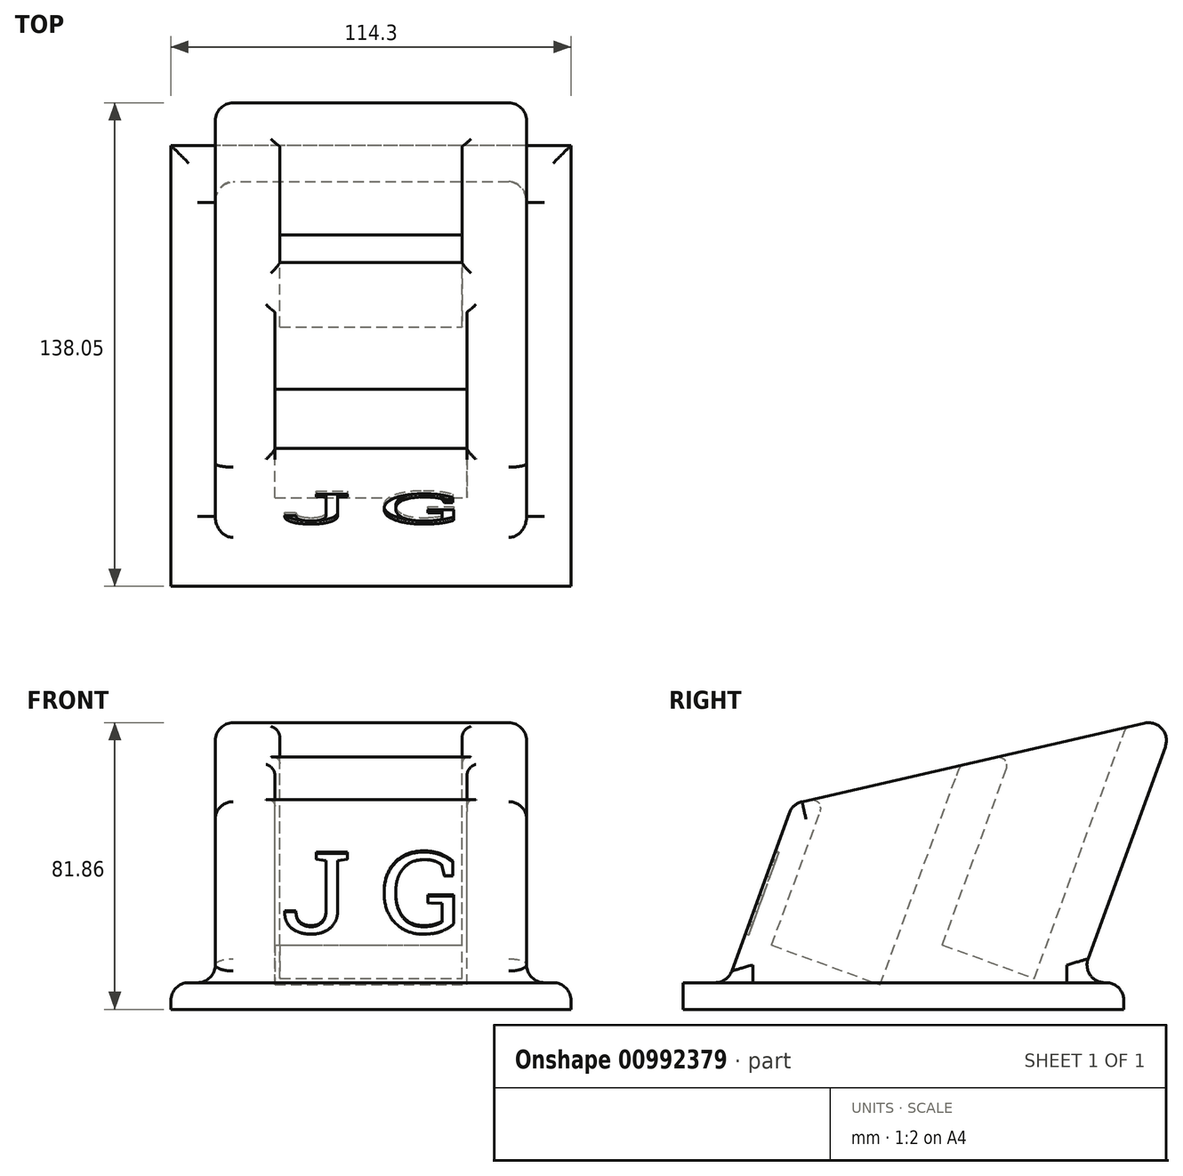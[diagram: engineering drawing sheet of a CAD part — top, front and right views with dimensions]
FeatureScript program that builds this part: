
annotation { "Feature Type Name" : "Feature", "Feature Type Description" : "" }
export const myFeature = defineFeature(function(context is Context, id is Id, definition is map)
    precondition{}
    {
        {
            var Q0;
            Q0=qCreatedBy(makeId("Right.planeOp"),FACE);
            var sketch = newSketch(context, id + "F0", { "sketchPlane" : qUnion([Q0])});
            skLineSegment(sketch, "E0.bottom", {"start": v(-88.9, 0) * mm, "end": v(88.9, 0) * mm});
            skLineSegment(sketch, "E0.left", {"start": v(-88.9, 0) * mm, "end": v(-88.9, 7.62) * mm});
            skLineSegment(sketch, "E0.right", {"start": v(88.9, 0) * mm, "end": v(88.9, 7.62) * mm});
            skLineSegment(sketch, "E1", {"start": v(-88.9, 7.62) * mm, "end": v(88.9, 7.62) * mm});
            skLineSegment(sketch, "E2", {"start": v(76.2, 7.62) * mm, "end": v(103.93, 83.82) * mm});
            skLineSegment(sketch, "E3", {"start": v(-76.2, 7.62) * mm, "end": v(-62.33, 45.72) * mm});
            skLineSegment(sketch, "E4", {"start": v(-62.33, 45.72) * mm, "end": v(103.93, 83.82) * mm});
            skSolve(sketch);
        }
        {
            var Q0;
            Q0=makeQuery(id+"F0.imprint","IMPRINT",FACE,{"disambiguationData":[TD([[makeQuery(id+"F0.imprint","IMPRINT",EDGE,{"derivedFrom":sQuery(id+"F0.wireOp",EDGE,"E0.bottom")}),1.0]])]});
            extrude(context, id + "F1", {"entities" : qUnion([Q0]), "depth" : 114.3 * mm, "offsetDistance" : 25.4 * mm, "symmetric" : true});
        }
        {
            var Q0;
            {var subQ0=sQuery(id+"F0.wireOp",EDGE,"E2");Q0=makeQuery(id+"F0.imprint","IMPRINT",FACE,{"disambiguationData":[TD([[makeQuery(id+"F0.imprint","IMPRINT",EDGE,{"derivedFrom":subQ0}),1.0]])]});}
            extrude(context, id + "F2", {"entities" : qUnion([Q0]), "operationType" : NewBodyOperationType.ADD, "depth" : 88.9 * mm, "offsetDistance" : 25.4 * mm, "symmetric" : true});
        }
        {
            var Q0;
            Q0=makeQuery(id+"F2.opExtrude","SWEPT_EDGE",EDGE,{"disambiguationData":[OSD([sQuery(id+"F0.wireOp",EDGE,"E2"),sQuery(id+"F0.wireOp",EDGE,"E4")])]});
            var Q1;
            Q1=sQuery(id+"F0.wireOp",EDGE,"E2");
            cPlane(context, id + "F3", {"entities" : qUnion([Q0, Q1]), "cplaneType" : CPlaneType.LINE_ANGLE, "offset" : 25.4 * mm, "angle" : 90 * degree, "width" : 152.4 * mm, "height" : 152.4 * mm});
        }
        {
            var Q0;
            Q0=makeQuery(id+"F2.opExtrude","SWEPT_FACE",FACE,{"disambiguationData":[OSD([sQuery(id+"F0.wireOp",EDGE,"E4")])]});
            var sketch = newSketch(context, id + "F4", { "sketchPlane" : qUnion([Q0])});
            skLineSegment(sketch, "E5.bottom", {"start": v(20.96, -42.93) * mm, "end": v(-20.96, -42.93) * mm});
            skSolve(sketch);
        }
        {
            var Q0;
            Q0=qCreatedBy(id+"F3.planeOp",FACE);
            var sketch = newSketch(context, id + "F5", { "sketchPlane" : qUnion([Q0])});
            skLineSegment(sketch, "E6.0", {"start": v(20.96, 67.81) * mm, "end": v(-20.96, 67.81) * mm});
            skLineSegment(sketch, "E7", {"start": v(-20.96, 67.81) * mm, "end": v(-20.96, 59.43) * mm});
            skLineSegment(sketch, "E8", {"start": v(-20.96, 59.43) * mm, "end": v(20.96, 59.43) * mm});
            skLineSegment(sketch, "E9", {"start": v(20.95, 59.43) * mm, "end": v(20.95, 67.81) * mm});
            skSolve(sketch);
        }
        {
            var Q0;
            Q0 = qSketchRegion(id + "F5", true);
            extrude(context, id + "F6", {"entities" : qUnion([Q0]), "operationType" : NewBodyOperationType.REMOVE, "depth" : 110.74 * mm, "offsetDistance" : 25.4 * mm});
        }
        {
            var Q0;
            {var subQ0=sQuery(id+"F0.wireOp",EDGE,"E4");Q0=makeQuery(id+"F4.imprint","IMPRINT",FACE,{"disambiguationData":[TD([[makeQuery(id+"F4.imprint","IMPRINT",EDGE,{"derivedFrom":makeQuery(id+"F2.opExtrude","CAP_EDGE",EDGE,{"disambiguationData":[OSD([subQ0])],"isStart":true})}),-1.0]])]});}
            var sketch = newSketch(context, id + "F7", { "sketchPlane" : qUnion([Q0])});
            skLineSegment(sketch, "E10", {"start": v(-23.5, -20.24) * mm, "end": v(23.5, -20.24) * mm});
            skSolve(sketch);
        }
        {
            var Q0;
            Q0=qCreatedBy(id+"F3.planeOp",FACE);
            var sketch = newSketch(context, id + "F8", { "sketchPlane" : qUnion([Q0])});
            skLineSegment(sketch, "E11.0", {"start": v(-23.5, 48.77) * mm, "end": v(23.5, 48.77) * mm});
            skLineSegment(sketch, "E12", {"start": v(-23.5, 48.77) * mm, "end": v(-23.5, 27.94) * mm});
            skLineSegment(sketch, "E13", {"start": v(-23.5, 27.94) * mm, "end": v(23.5, 27.94) * mm});
            skLineSegment(sketch, "E14", {"start": v(23.5, 27.94) * mm, "end": v(23.5, 48.77) * mm});
            skSolve(sketch);
        }
        {
            var Q0;
            Q0 = qSketchRegion(id + "F8", true);
            extrude(context, id + "F9", {"entities" : qUnion([Q0]), "operationType" : NewBodyOperationType.REMOVE, "depth" : 112.27 * mm, "offsetDistance" : 25.4 * mm});
        }
        {
            var Q0;
            {var subQ0=sQuery(id+"F0.wireOp",EDGE,"E4");Q0=makeQuery(id+"F4.imprint","IMPRINT",FACE,{"disambiguationData":[TD([[makeQuery(id+"F4.imprint","IMPRINT",EDGE,{"derivedFrom":makeQuery(id+"F2.opExtrude","CAP_EDGE",EDGE,{"disambiguationData":[OSD([subQ0])],"isStart":true})}),-1.0]])]});}
            var sketch = newSketch(context, id + "F10", { "sketchPlane" : qUnion([Q0])});
            skLineSegment(sketch, "E15", {"start": v(-27.43, 17.27) * mm, "end": v(27.43, 17.27) * mm});
            skLineSegment(sketch, "E16", {"start": v(0, 85.1) * mm, "end": v(0, -16.61) * mm, "construction": true});
            skSolve(sketch);
        }
        {
            var Q0;
            Q0=qCreatedBy(id+"F3.planeOp",FACE);
            var sketch = newSketch(context, id + "F11", { "sketchPlane" : qUnion([Q0])});
            skLineSegment(sketch, "E17.0", {"start": v(-27.43, 17.28) * mm, "end": v(27.43, 17.28) * mm});
            skLineSegment(sketch, "E18", {"start": v(-27.43, 17.28) * mm, "end": v(-27.43, -15.74) * mm});
            skLineSegment(sketch, "E19", {"start": v(-27.43, -15.74) * mm, "end": v(27.43, -15.74) * mm});
            skLineSegment(sketch, "E20", {"start": v(27.43, -15.74) * mm, "end": v(27.43, 17.28) * mm});
            skSolve(sketch);
        }
        {
            var Q0;
            Q0 = qSketchRegion(id + "F11", true);
            extrude(context, id + "F12", {"entities" : qUnion([Q0]), "operationType" : NewBodyOperationType.REMOVE, "depth" : 101.1 * mm, "offsetDistance" : 25.4 * mm});
        }
        {
            var Q0;
            {var subQ0=sQuery(id+"F0.wireOp",EDGE,"E4");Q0=makeQuery(id+"F4.imprint","IMPRINT",FACE,{"disambiguationData":[TD([[makeQuery(id+"F4.imprint","IMPRINT",EDGE,{"derivedFrom":makeQuery(id+"F2.opExtrude","CAP_EDGE",EDGE,{"disambiguationData":[OSD([subQ0])],"isStart":true})}),-1.0]])]});}
            var sketch = newSketch(context, id + "F13", { "sketchPlane" : qUnion([Q0])});
            skLineSegment(sketch, "E21", {"start": v(-26.04, 71.84) * mm, "end": v(26.04, 71.84) * mm});
            skSolve(sketch);
        }
        {
            var Q0;
            Q0=qCreatedBy(id+"F3.planeOp",FACE);
            var sketch = newSketch(context, id + "F14", { "sketchPlane" : qUnion([Q0])});
            skLineSegment(sketch, "E22.0", {"start": v(-26.04, -28.54) * mm, "end": v(26.04, -28.54) * mm});
            skLineSegment(sketch, "E23", {"start": v(-26.03, -28.54) * mm, "end": v(-26.03, -56.48) * mm});
            skLineSegment(sketch, "E24", {"start": v(-26.03, -56.48) * mm, "end": v(26.04, -56.48) * mm});
            skLineSegment(sketch, "E25", {"start": v(26.04, -56.48) * mm, "end": v(26.04, -28.54) * mm});
            skSolve(sketch);
        }
        {
            var Q0;
            Q0 = qSketchRegion(id + "F14", true);
            extrude(context, id + "F15", {"entities" : qUnion([Q0]), "operationType" : NewBodyOperationType.REMOVE, "depth" : 84.33 * mm, "offsetDistance" : 25.4 * mm});
        }
        {
            var Q0;
            Q0=makeQuery(id+"F2.opExtrude","CAP_EDGE",EDGE,{"disambiguationData":[OSD([sQuery(id+"F0.wireOp",EDGE,"E4")])],"isStart":false});
            var Q1;
            Q1=makeQuery(id+"F2.opExtrude","SWEPT_EDGE",EDGE,{"disambiguationData":[OSD([sQuery(id+"F0.wireOp",EDGE,"E3"),sQuery(id+"F0.wireOp",EDGE,"E4")])]});
            var Q2;
            Q2=makeQuery(id+"F2.opExtrude","CAP_FACE",FACE,{"disambiguationData":[OSD([sQuery(id+"F0.wireOp",EDGE,"E1"),sQuery(id+"F0.wireOp",EDGE,"E2"),sQuery(id+"F0.wireOp",EDGE,"E3"),sQuery(id+"F0.wireOp",EDGE,"E4")])],"isStart":false});
            var Q3;
            Q3=makeQuery(id+"F2.opExtrude","SWEPT_EDGE",EDGE,{"disambiguationData":[OSD([sQuery(id+"F0.wireOp",EDGE,"E2"),sQuery(id+"F0.wireOp",EDGE,"E4")])]});
            var Q4;
            Q4=makeQuery(id+"F2.opExtrude","CAP_FACE",FACE,{"disambiguationData":[OSD([sQuery(id+"F0.wireOp",EDGE,"E1"),sQuery(id+"F0.wireOp",EDGE,"E2"),sQuery(id+"F0.wireOp",EDGE,"E3"),sQuery(id+"F0.wireOp",EDGE,"E4")])],"isStart":true});
            var Q5;
            Q5=makeQuery(id+"F1.opExtrude","SWEPT_FACE",FACE,{"disambiguationData":[OSD([sQuery(id+"F0.wireOp",EDGE,"E1")])]});
            fillet(context, id + "F16", {"entities" : qUnion([Q0, Q1, Q2, Q3, Q4, Q5]), "tangentPropagation" : true, "radius" : 5.08 * mm, "defaultsChanged" : false, "vertexSettings" : [], "allowEdgeOverflow" : false});
        }
        {
            var Q0;
            Q0=makeQuery(id+"F15.boolean.opBoolean","INTERSECT",EDGE,{"derivedFrom":[makeQuery(id+"F2.opExtrude","SWEPT_FACE",FACE,{"disambiguationData":[OSD([sQuery(id+"F0.wireOp",EDGE,"E4")])]}),makeQuery(id+"F15.opExtrude","SWEPT_FACE",FACE,{"disambiguationData":[OSD([sQuery(id+"F14.wireOp",EDGE,"E22.0")])]})]});
            var Q1;
            Q1=makeQuery(id+"F15.boolean.opBoolean","INTERSECT",EDGE,{"derivedFrom":[makeQuery(id+"F2.opExtrude","SWEPT_FACE",FACE,{"disambiguationData":[OSD([sQuery(id+"F0.wireOp",EDGE,"E4")])]}),makeQuery(id+"F15.opExtrude","SWEPT_FACE",FACE,{"disambiguationData":[OSD([sQuery(id+"F14.wireOp",EDGE,"E24")])]})]});
            var Q2;
            Q2=makeQuery(id+"F15.boolean.opBoolean","INTERSECT",EDGE,{"derivedFrom":[makeQuery(id+"F2.opExtrude","SWEPT_FACE",FACE,{"disambiguationData":[OSD([sQuery(id+"F0.wireOp",EDGE,"E4")])]}),makeQuery(id+"F15.opExtrude","SWEPT_FACE",FACE,{"disambiguationData":[OSD([sQuery(id+"F14.wireOp",EDGE,"E25")])]})]});
            var Q3;
            Q3=makeQuery(id+"F15.boolean.opBoolean","INTERSECT",EDGE,{"derivedFrom":[makeQuery(id+"F2.opExtrude","SWEPT_FACE",FACE,{"disambiguationData":[OSD([sQuery(id+"F0.wireOp",EDGE,"E4")])]}),makeQuery(id+"F15.opExtrude","SWEPT_FACE",FACE,{"disambiguationData":[OSD([sQuery(id+"F14.wireOp",EDGE,"E23")])]})]});
            var Q4;
            Q4=makeQuery(id+"F12.boolean.opBoolean","INTERSECT",EDGE,{"derivedFrom":[makeQuery(id+"F2.opExtrude","SWEPT_FACE",FACE,{"disambiguationData":[OSD([sQuery(id+"F0.wireOp",EDGE,"E4")])]}),makeQuery(id+"F12.opExtrude","SWEPT_FACE",FACE,{"disambiguationData":[OSD([sQuery(id+"F11.wireOp",EDGE,"E18")])]})]});
            var Q5;
            Q5=makeQuery(id+"F12.boolean.opBoolean","INTERSECT",EDGE,{"derivedFrom":[makeQuery(id+"F2.opExtrude","SWEPT_FACE",FACE,{"disambiguationData":[OSD([sQuery(id+"F0.wireOp",EDGE,"E4")])]}),makeQuery(id+"F12.opExtrude","SWEPT_FACE",FACE,{"disambiguationData":[OSD([sQuery(id+"F11.wireOp",EDGE,"E19")])]})]});
            var Q6;
            Q6=makeQuery(id+"F12.boolean.opBoolean","INTERSECT",EDGE,{"derivedFrom":[makeQuery(id+"F2.opExtrude","SWEPT_FACE",FACE,{"disambiguationData":[OSD([sQuery(id+"F0.wireOp",EDGE,"E4")])]}),makeQuery(id+"F12.opExtrude","SWEPT_FACE",FACE,{"disambiguationData":[OSD([sQuery(id+"F11.wireOp",EDGE,"E20")])]})]});
            var Q7;
            Q7=makeQuery(id+"F12.boolean.opBoolean","INTERSECT",EDGE,{"derivedFrom":[makeQuery(id+"F2.opExtrude","SWEPT_FACE",FACE,{"disambiguationData":[OSD([sQuery(id+"F0.wireOp",EDGE,"E4")])]}),makeQuery(id+"F12.opExtrude","SWEPT_FACE",FACE,{"disambiguationData":[OSD([sQuery(id+"F11.wireOp",EDGE,"E17.0")])]})]});
            var Q8;
            Q8=makeQuery(id+"F9.boolean.opBoolean","INTERSECT",EDGE,{"derivedFrom":[makeQuery(id+"F2.opExtrude","SWEPT_FACE",FACE,{"disambiguationData":[OSD([sQuery(id+"F0.wireOp",EDGE,"E4")])]}),makeQuery(id+"F9.opExtrude","SWEPT_FACE",FACE,{"disambiguationData":[OSD([sQuery(id+"F8.wireOp",EDGE,"E13")])]})]});
            var Q9;
            Q9=makeQuery(id+"F9.boolean.opBoolean","INTERSECT",EDGE,{"derivedFrom":[makeQuery(id+"F2.opExtrude","SWEPT_FACE",FACE,{"disambiguationData":[OSD([sQuery(id+"F0.wireOp",EDGE,"E4")])]}),makeQuery(id+"F9.opExtrude","SWEPT_FACE",FACE,{"disambiguationData":[OSD([sQuery(id+"F8.wireOp",EDGE,"E14")])]})]});
            var Q10;
            Q10=makeQuery(id+"F9.boolean.opBoolean","INTERSECT",EDGE,{"derivedFrom":[makeQuery(id+"F2.opExtrude","SWEPT_FACE",FACE,{"disambiguationData":[OSD([sQuery(id+"F0.wireOp",EDGE,"E4")])]}),makeQuery(id+"F9.opExtrude","SWEPT_FACE",FACE,{"disambiguationData":[OSD([sQuery(id+"F8.wireOp",EDGE,"E11.0")])]})]});
            var Q11;
            Q11=makeQuery(id+"F9.boolean.opBoolean","INTERSECT",EDGE,{"derivedFrom":[makeQuery(id+"F2.opExtrude","SWEPT_FACE",FACE,{"disambiguationData":[OSD([sQuery(id+"F0.wireOp",EDGE,"E4")])]}),makeQuery(id+"F9.opExtrude","SWEPT_FACE",FACE,{"disambiguationData":[OSD([sQuery(id+"F8.wireOp",EDGE,"E12")])]})]});
            var Q12;
            Q12=makeQuery(id+"F6.boolean.opBoolean","INTERSECT",EDGE,{"derivedFrom":[makeQuery(id+"F2.opExtrude","SWEPT_FACE",FACE,{"disambiguationData":[OSD([sQuery(id+"F0.wireOp",EDGE,"E4")])]}),makeQuery(id+"F6.opExtrude","SWEPT_FACE",FACE,{"disambiguationData":[OSD([sQuery(id+"F5.wireOp",EDGE,"E8")])]})]});
            var Q13;
            Q13=makeQuery(id+"F6.boolean.opBoolean","INTERSECT",EDGE,{"derivedFrom":[makeQuery(id+"F2.opExtrude","SWEPT_FACE",FACE,{"disambiguationData":[OSD([sQuery(id+"F0.wireOp",EDGE,"E4")])]}),makeQuery(id+"F6.opExtrude","SWEPT_FACE",FACE,{"disambiguationData":[OSD([sQuery(id+"F5.wireOp",EDGE,"E7")])]})]});
            var Q14;
            Q14=makeQuery(id+"F6.boolean.opBoolean","INTERSECT",EDGE,{"derivedFrom":[makeQuery(id+"F2.opExtrude","SWEPT_FACE",FACE,{"disambiguationData":[OSD([sQuery(id+"F0.wireOp",EDGE,"E4")])]}),makeQuery(id+"F6.opExtrude","SWEPT_FACE",FACE,{"disambiguationData":[OSD([sQuery(id+"F5.wireOp",EDGE,"E9")])]})]});
            var Q15;
            Q15=makeQuery(id+"F6.boolean.opBoolean","INTERSECT",EDGE,{"derivedFrom":[makeQuery(id+"F2.opExtrude","SWEPT_FACE",FACE,{"disambiguationData":[OSD([sQuery(id+"F0.wireOp",EDGE,"E4")])]}),makeQuery(id+"F6.opExtrude","SWEPT_FACE",FACE,{"disambiguationData":[OSD([sQuery(id+"F5.wireOp",EDGE,"E6.0")])]})]});
            fillet(context, id + "F17", {"entities" : qUnion([Q0, Q1, Q2, Q3, Q4, Q5, Q6, Q7, Q8, Q9, Q10, Q11, Q12, Q13, Q14, Q15]), "tangentPropagation" : true, "radius" : 2.54 * mm, "defaultsChanged" : false, "vertexSettings" : [], "allowEdgeOverflow" : false});
        }
        {
            var Q0;
            Q0=qCreatedBy(id+"F3.planeOp",FACE);
            var sketch = newSketch(context, id + "F18", { "sketchPlane" : qUnion([Q0])});
            skLineSegment(sketch, "E26.bottom", {"start": v(-89.05, 25.44) * mm, "end": v(102.74, 25.44) * mm});
            skLineSegment(sketch, "E26.top", {"start": v(-89.05, 102.91) * mm, "end": v(102.74, 102.91) * mm});
            skLineSegment(sketch, "E26.left", {"start": v(-89.05, 25.44) * mm, "end": v(-89.05, 102.91) * mm});
            skLineSegment(sketch, "E26.right", {"start": v(102.74, 25.44) * mm, "end": v(102.74, 102.91) * mm});
            skSolve(sketch);
        }
        {
            var Q0;
            Q0=makeQuery(id+"F18.imprint","IMPRINT",FACE,{"disambiguationData":[TD([[makeQuery(id+"F18.imprint","IMPRINT",EDGE,{"derivedFrom":sQuery(id+"F18.wireOp",EDGE,"E26.bottom")}),1.0]])]});
            var Q1;
            Q1=makeQuery(id+"F1.opExtrude","SWEPT_FACE",FACE,{"disambiguationData":[OSD([sQuery(id+"F0.wireOp",EDGE,"E1")])]});
            extrude(context, id + "F19", {"entities" : qUnion([Q0]), "operationType" : NewBodyOperationType.REMOVE, "endBound" : BoundingType.UP_TO_SURFACE, "depth" : 25.4 * mm, "endBoundEntityFace" : qUnion([Q1]), "offsetDistance" : 25.4 * mm});
        }
        {
            var Q0;
            Q0=makeQuery(id+"F19.boolean.opBoolean","MERGE",FACE,{"derivedFrom":[makeQuery(id+"F1.opExtrude","SWEPT_FACE",FACE,{"disambiguationData":[OSD([sQuery(id+"F0.wireOp",EDGE,"E1")])]})],"fromTools":[makeQuery(id+"F19.opExtrude","CAP_FACE",FACE,{"disambiguationData":[OSD([sQuery(id+"F18.wireOp",EDGE,"E26.bottom"),sQuery(id+"F18.wireOp",EDGE,"E26.top"),sQuery(id+"F18.wireOp",EDGE,"E26.left"),sQuery(id+"F18.wireOp",EDGE,"E26.right")])],"isStart":false})]});
            var sketch = newSketch(context, id + "F20", { "sketchPlane" : qUnion([Q0])});
            skLineSegment(sketch, "E27.bottom", {"start": v(-111.8, -116.85) * mm, "end": v(163.3, -116.85) * mm});
            skLineSegment(sketch, "E27.top", {"start": v(-111.8, -37) * mm, "end": v(163.3, -37) * mm});
            skLineSegment(sketch, "E27.left", {"start": v(-111.8, -116.85) * mm, "end": v(-111.8, -37) * mm});
            skLineSegment(sketch, "E27.right", {"start": v(163.3, -116.85) * mm, "end": v(163.3, -37) * mm});
            skSolve(sketch);
        }
        {
            var Q0;
            Q0 = qSketchRegion(id + "F20", true);
            extrude(context, id + "F21", {"entities" : qUnion([Q0]), "operationType" : NewBodyOperationType.REMOVE, "oppositeDirection" : true, "depth" : 25.4 * mm, "offsetDistance" : 25.4 * mm});
        }
        {
            var Q0;
            Q0=makeQuery(id+"F21.boolean.opBoolean","COPY",EDGE,{"derivedFrom":makeQuery(id+"F21.opExtrude","CAP_EDGE",EDGE,{"disambiguationData":[OSD([sQuery(id+"F20.wireOp",EDGE,"E27.top")])],"isStart":true})});
            var Q1;
            Q1=makeQuery(id+"F19.boolean.opBoolean","INTERSECT",EDGE,{"derivedFrom":[makeQuery(id+"F2.opExtrude","CAP_FACE",FACE,{"disambiguationData":[OSD([sQuery(id+"F0.wireOp",EDGE,"E1"),sQuery(id+"F0.wireOp",EDGE,"E2"),sQuery(id+"F0.wireOp",EDGE,"E3"),sQuery(id+"F0.wireOp",EDGE,"E4")])],"isStart":false}),makeQuery(id+"F19.opExtrude","SWEPT_FACE",FACE,{"disambiguationData":[OSD([sQuery(id+"F18.wireOp",EDGE,"E26.bottom")])]})]});
            var Q2;
            Q2=makeQuery(id+"F19.boolean.opBoolean","COPY",EDGE,{"derivedFrom":makeQuery(id+"F19.opExtrude","CAP_EDGE",EDGE,{"disambiguationData":[OSD([sQuery(id+"F18.wireOp",EDGE,"E26.bottom")])],"isStart":false})});
            fillet(context, id + "F22", {"entities" : qUnion([Q0, Q1, Q2]), "tangentPropagation" : true, "radius" : 5.08 * mm, "defaultsChanged" : false, "vertexSettings" : [], "allowEdgeOverflow" : false});
        }
        {
            var Q0;
            Q0=makeQuery(id+"F19.boolean.opBoolean","COPY",FACE,{"derivedFrom":makeQuery(id+"F19.opExtrude","SWEPT_FACE",FACE,{"disambiguationData":[OSD([sQuery(id+"F18.wireOp",EDGE,"E26.bottom")])]})});
            var sketch = newSketch(context, id + "F23", { "sketchPlane" : qUnion([Q0])});
            skText(sketch, "E28", { "text": "J G", "fontName": "RobotoSlab-Regular.ttf"});
            skLineSegment(sketch, "E29", {"start": v(0, 50.44) * mm, "end": v(0, -4.62) * mm, "construction": true});
            const initialGuessF23  = {"E28": [-0.02574, 0.01397, 1, 0, 0.0249]};
            skSetInitialGuess(sketch, initialGuessF23);
            skSolve(sketch);
        }
        {
            var Q0;
            Q0 = qSketchRegion(id + "F23", true);
            extrude(context, id + "F24", {"entities" : qUnion([Q0]), "operationType" : NewBodyOperationType.REMOVE, "oppositeDirection" : true, "depth" : 1.02 * mm, "offsetDistance" : 25.4 * mm});
        }
    });
